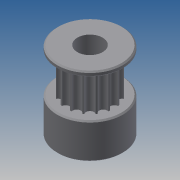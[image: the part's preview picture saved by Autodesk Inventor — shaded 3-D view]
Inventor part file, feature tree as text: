
AUTODESK INVENTOR PART (.ipt)
format: ipt  version: 2013 (Build 170138000, 138)  size: 161,280 bytes
history: native  units: mm
features: extrude x5, sketch x5, pattern_circular x1, chamfer x1
ambient origin geometry x8: Origin, YZ Plane, XZ Plane, XY Plane, X Axis, Y Axis, Z Axis, Center Point
bodies: Solid1 (feature_tree)
feature tree (12):
  extrude  "Extrusion1"  Depth=7.5mm TaperAngle=0.0deg
  extrude  "Extrusion2"  Depth=9.0mm TaperAngle=0.0deg
  pattern_circular  "Circular Pattern1"  Count=16 Angle=360.0deg
  extrude  "Extrusion3"  Depth=1.0mm TaperAngle=0.0deg
  extrude  "Extrusion4"  Depth=5.0mm
  extrude  "Extrusion5"  Depth=0.25mm TaperAngle=45.0deg
  chamfer  "Chamfer1"  [1 undecoded]
  sketch  "Sketch1"  dims[d0=9.683083mm d2=7.5mm d3=0.0mm]
  sketch  "Sketch2"  dims[d4=1.59mm d6=9.0mm d7=0.0mm d8=160.0mm d9=360.0deg]
  sketch  "Sketch3"  dims[d11=13.0mm d13=1.0mm d14=0.0mm]
  sketch  "Sketch4"  dims[d15=7.0mm d16=0.0mm d17=5.0mm]
  sketch  "Sketch5"  dims[d19=7.0mm d20=0.0mm d21=0.25mm d22=2.0mm d23=45.0deg]
note: 1 required parameter value undecoded (feature->parameter linkage not recoverable at this tier; creation-order binding heuristic only, values carry confidence <= 0.55)
